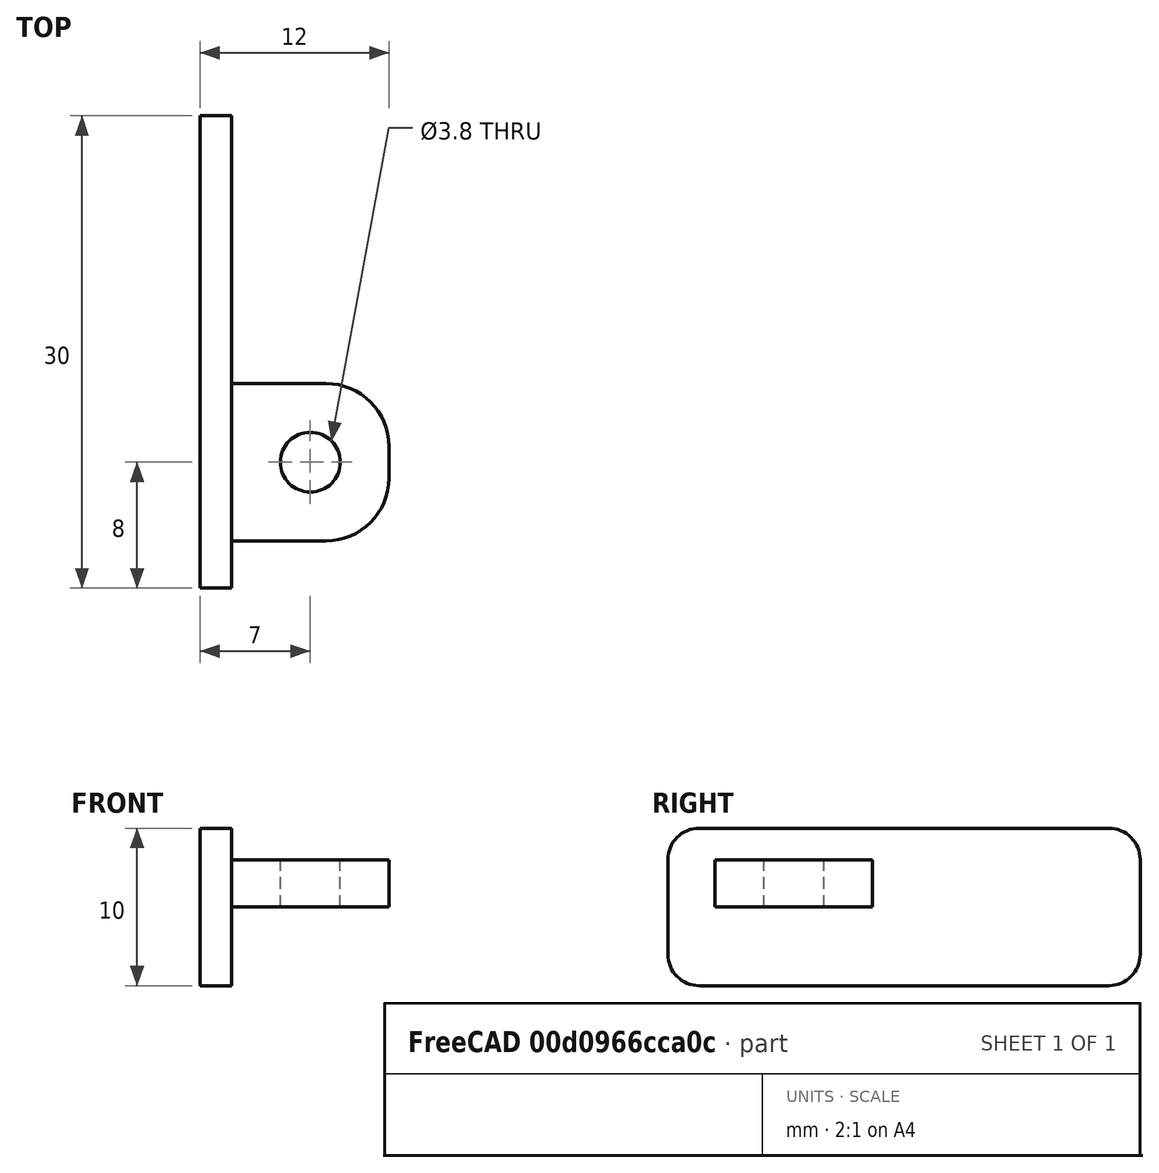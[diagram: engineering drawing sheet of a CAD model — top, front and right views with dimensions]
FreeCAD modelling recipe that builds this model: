
FCSTD DOCUMENT  (FreeCAD 0.19R23578 (Git))
Label: battery_lock
License: All rights reserved
LicenseURL: http://en.wikipedia.org/wiki/All_rights_reserved
objects: Part::Box×2, Part::Fillet×2, Part::Cylinder×1, Part::MultiFuse×1, Part::Cut×1
note: 7 computed .brp shape members not serialized (recipe doc carries the construction recipe); baked Part::Feature solids carry a one-line shape summary decoded from their .brp

FEATURE [Part::Box] Box  label="bottom"
  AttacherType = Attacher::AttachEngine3D
  Height = 3
  Length = 10
  Placement = pos=(-5,-5,0) rot=(0,0,1;0rad)
  Width = 10
  expr: .Placement.Base.y = -Width / 2
  expr: .Placement.Base.x = -Length / 2
FEATURE [Part::Fillet] Fillet  label="bottom fillet"
  Base = -> Box
  Edges = 2 edges r=4: [Edge5,Edge7]
FEATURE [Part::Cylinder] Cylinder  label="hole"
  Angle = 360
  AttacherType = Attacher::AttachEngine3D
  Height = 10
  Radius = 1.9
FEATURE [Part::Box] Box001  label="wall"
  AttacherType = Attacher::AttachEngine3D
  Height = 10
  Length = 2
  Placement = pos=(-7,-8,-5) rot=(0,0,1;0rad)
  Width = 30
  expr: .Placement.Base.z = -Height / 2
  expr: .Placement.Base.x = -<<bottom>>.Length / 2 - Length
FEATURE [Part::Fillet] Fillet001  label="wall fillet"
  Base = -> Box001
  Edges = 4 edges r=2: [Edge9,Edge10,Edge11,Edge12]
FEATURE [Part::MultiFuse] Fusion  label="lock fusion"
  Shapes = -> [Fillet001,Fillet]
FEATURE [Part::Cut] Cut  label="lock cut"
  Base = -> Fusion
  Tool = -> Cylinder
